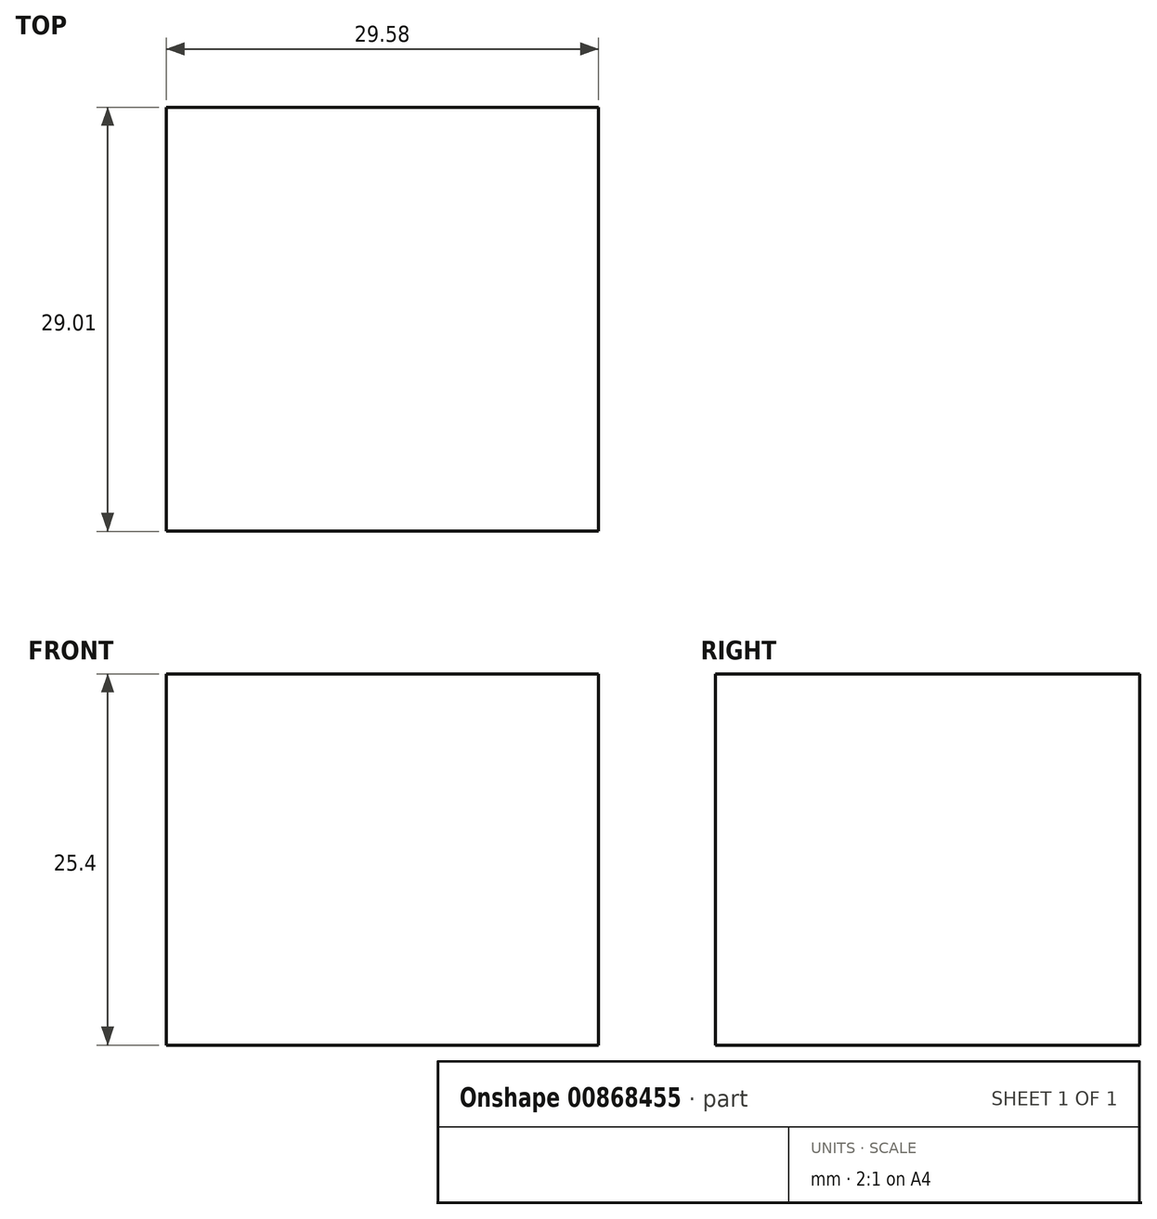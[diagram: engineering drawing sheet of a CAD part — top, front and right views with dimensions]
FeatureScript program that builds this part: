
annotation { "Feature Type Name" : "Feature", "Feature Type Description" : "" }
export const myFeature = defineFeature(function(context is Context, id is Id, definition is map)
    precondition{}
    {
        {
            var Q0;
            Q0=qCreatedBy(makeId("Top.planeOp"),FACE);
            var sketch = newSketch(context, id + "F0", { "sketchPlane" : qUnion([Q0])});
            skLineSegment(sketch, "E0.bottom", {"start": v(-49.01, 34.98) * mm, "end": v(-19.43, 34.98) * mm});
            skLineSegment(sketch, "E0.top", {"start": v(-49.01, 5.97) * mm, "end": v(-19.43, 5.97) * mm});
            skLineSegment(sketch, "E0.left", {"start": v(-49.01, 34.98) * mm, "end": v(-49.01, 5.97) * mm});
            skLineSegment(sketch, "E0.right", {"start": v(-19.43, 34.98) * mm, "end": v(-19.43, 5.97) * mm});
            skLineSegment(sketch, "E1.bottom", {"start": v(-19.43, 5.97) * mm, "end": v(-49.01, 5.97) * mm});
            skLineSegment(sketch, "E1.top", {"start": v(-19.43, 34.98) * mm, "end": v(-49.01, 34.98) * mm});
            skLineSegment(sketch, "E1.left", {"start": v(-19.43, 5.97) * mm, "end": v(-19.43, 34.98) * mm});
            skLineSegment(sketch, "E1.right", {"start": v(-49.01, 5.97) * mm, "end": v(-49.01, 34.98) * mm});
            skSolve(sketch);
        }
        {
            var Q0;
            Q0 = qSketchRegion(id + "F0", true);
            extrude(context, id + "F1", {"entities" : qUnion([Q0]), "depth" : 25.4 * mm, "offsetDistance" : 25.4 * mm});
        }
    });
